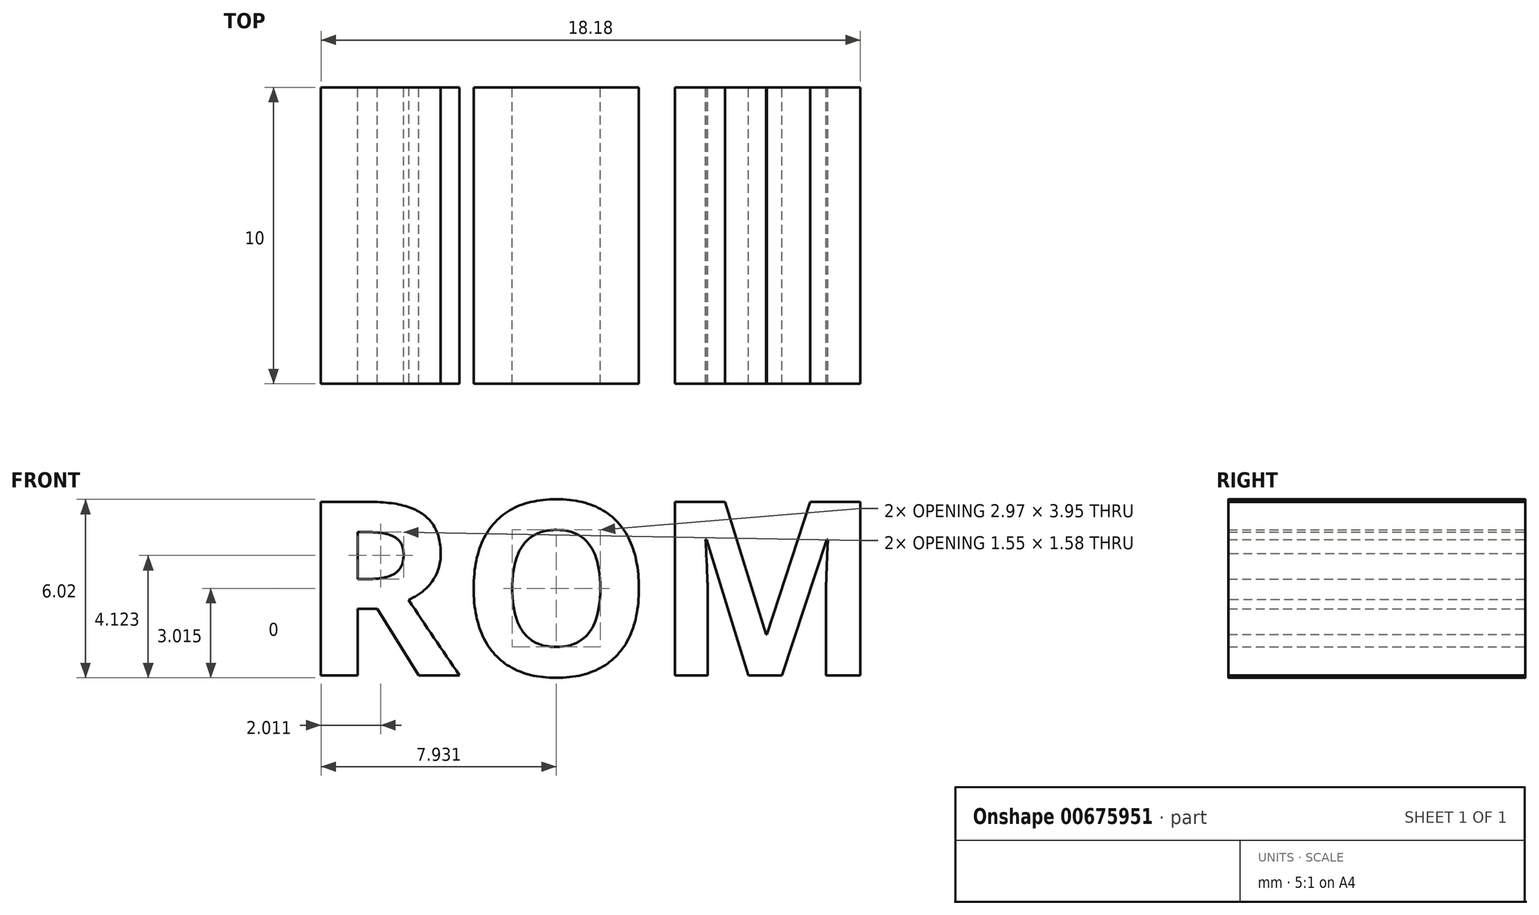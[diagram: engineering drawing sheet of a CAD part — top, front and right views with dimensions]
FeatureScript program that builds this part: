
annotation { "Feature Type Name" : "Feature", "Feature Type Description" : "" }
export const myFeature = defineFeature(function(context is Context, id is Id, definition is map)
    precondition{}
    {
        {
            var Q0;
            Q0=qCreatedBy(makeId("Front.planeOp"),FACE);
            var sketch = newSketch(context, id + "F0", { "sketchPlane" : qUnion([Q0])});
            skText(sketch, "E0", { "text": "ROM", "fontName": "OpenSans-Bold.ttf"});
            const initialGuessF0  = {"E0": [-0.01948, 0, 1, 0, 0.0059]};
            skSetInitialGuess(sketch, initialGuessF0);
            skSolve(sketch);
        }
        {
            var Q0;
            Q0=makeQuery(id+"F0.imprint","IMPRINT",FACE,{"disambiguationData":[TD([[makeQuery(id+"F0.imprint","IMPRINT",EDGE,{"derivedFrom":sQuery(id+"F0.wireOp",EDGE,"E0.sketch_text.stroke-0")}),-1.0]])]});
            var Q1;
            Q1=makeQuery(id+"F0.imprint","IMPRINT",FACE,{"disambiguationData":[TD([[makeQuery(id+"F0.imprint","IMPRINT",EDGE,{"derivedFrom":sQuery(id+"F0.wireOp",EDGE,"E0.sketch_text.stroke-19")}),-1.0]])]});
            var Q2;
            Q2=makeQuery(id+"F0.imprint","IMPRINT",FACE,{"disambiguationData":[TD([[makeQuery(id+"F0.imprint","IMPRINT",EDGE,{"derivedFrom":sQuery(id+"F0.wireOp",EDGE,"E0.sketch_text.stroke-33")}),-1.0]])]});
            extrude(context, id + "F1", {"entities" : qUnion([Q0, Q1, Q2]), "depth" : 10 * mm, "offsetDistance" : 25.4 * mm});
        }
        {
            var Q0;
            Q0 = qSketchRegion(id + "F0", true);
            extrude(context, id + "F2", {"entities" : qUnion([Q0]), "depth" : 10 * mm, "offsetDistance" : 25.4 * mm});
        }
    });
